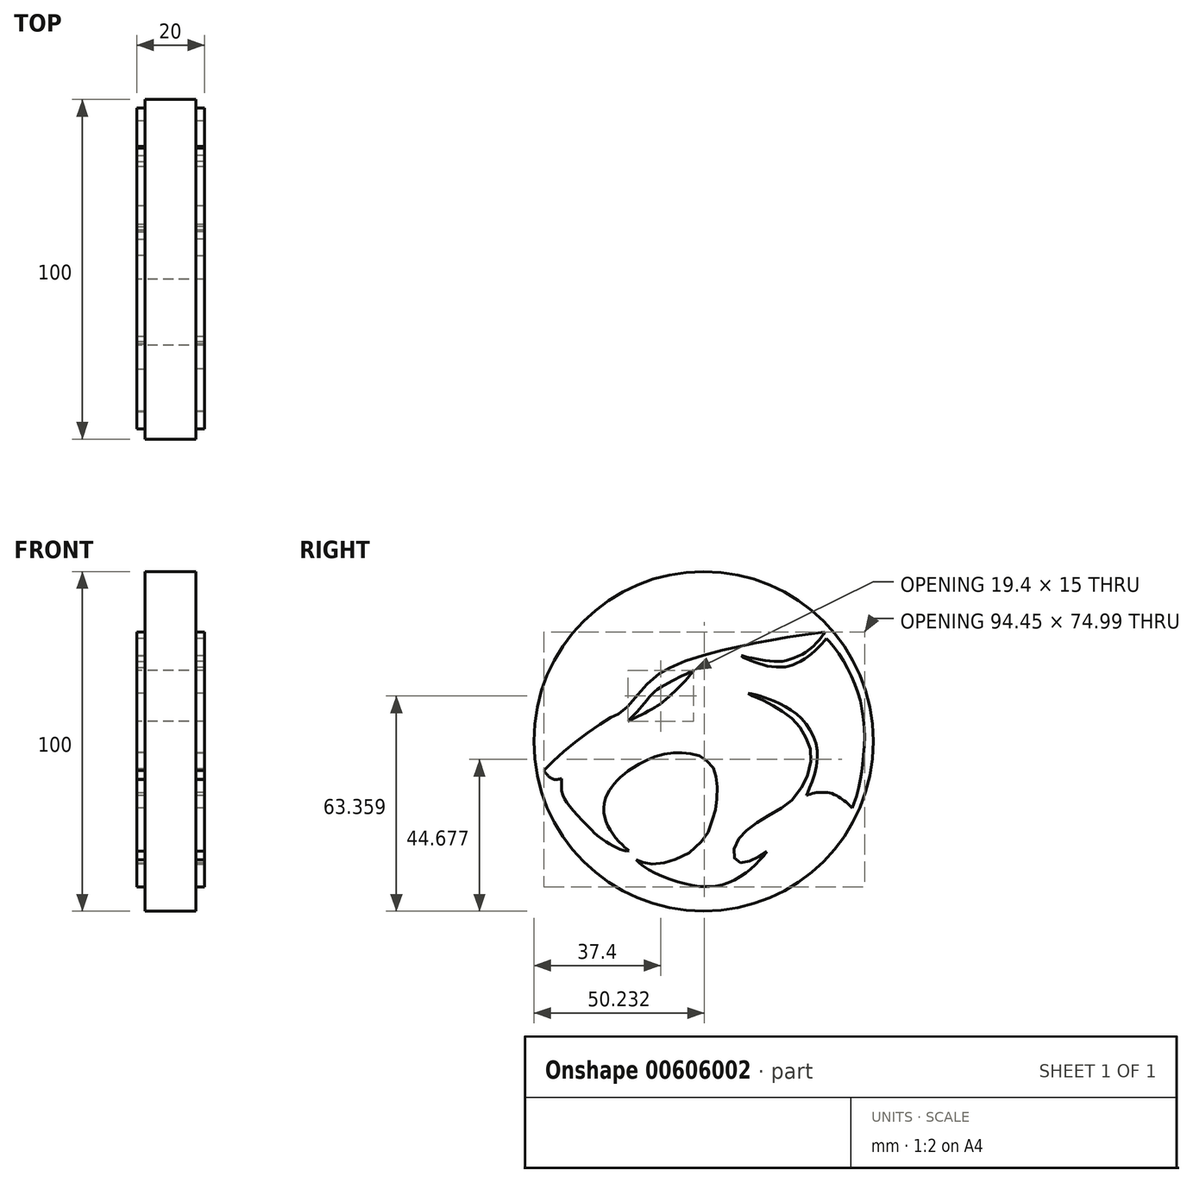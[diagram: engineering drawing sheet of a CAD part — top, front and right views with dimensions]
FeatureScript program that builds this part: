
annotation { "Feature Type Name" : "Feature", "Feature Type Description" : "" }
export const myFeature = defineFeature(function(context is Context, id is Id, definition is map)
    precondition{}
    {
        {
            var Q0;
            Q0=qCreatedBy(makeId("Right.planeOp"),FACE);
            var sketch = newSketch(context, id + "F0", { "sketchPlane" : qUnion([Q0])});
            skCircle(sketch, "E0", {"center": v(0, 0) * mm, "radius": 50 * mm});
            skFitSpline(sketch, "E1", {"points": [v(-47, -8.54) * mm, v(-41.27, -3.01) * mm, v(-33.53, 2.84) * mm, v(-26.97, 7.17) * mm, v(-24.14, 8.62) * mm, v(-17.89, 15.56) * mm, v(-14.85, 18.45) * mm, v(-13.16, 19.9) * mm, v(-4.4, 23.97) * mm, v(10.54, 27.95) * mm, v(20.91, 30.01) * mm, v(30.83, 31.56) * mm, v(35.72, 32.17) * mm], "startDerivative": vector(63.08, 64.93) * mm, "endDerivative": vector(65.23, 7.56) * mm});
            skFitSpline(sketch, "E2", {"points": [v(11.5, 25.21) * mm, v(13.68, 24.63) * mm, v(18.43, 23.8) * mm, v(22.9, 23.56) * mm, v(26.84, 24.6) * mm, v(31, 26.89) * mm, v(34.48, 30.36) * mm, v(35.72, 32.17) * mm], "startDerivative": vector(17.69, -5.27) * mm, "endDerivative": vector(9.54, 15.4) * mm});
            skFitSpline(sketch, "E3", {"points": [v(13.14, 14.17) * mm, v(14.47, 13.97) * mm, v(17.4, 13.1) * mm, v(20.48, 12) * mm, v(25.02, 9.67) * mm, v(29.51, 5.97) * mm, v(32.9, 0) * mm, v(33.22, -7.42) * mm, v(31.03, -14.2) * mm, v(30.28, -15.9) * mm], "startDerivative": vector(19.34, -1.93) * mm, "endDerivative": vector(-8.86, -19.07) * mm});
            skFitSpline(sketch, "E4", {"points": [v(-22.3, 5.86) * mm, v(-21.18, 7.13) * mm, v(-19.39, 8.93) * mm, v(-17.72, 10.93) * mm, v(-16.02, 13.02) * mm, v(-15.04, 14.03) * mm, v(-13.95, 15.09) * mm, v(-11.07, 16.79) * mm, v(-8.15, 18.4) * mm, v(-5.97, 19.46) * mm, v(-2.9, 20.86) * mm], "startDerivative": vector(12.35, 14.79) * mm, "endDerivative": vector(27.45, 12.44) * mm});
            skFitSpline(sketch, "E5", {"points": [v(-22.3, 5.86) * mm, v(-20.42, 6.83) * mm, v(-18.41, 7.74) * mm, v(-15.4, 9.41) * mm, v(-13.07, 10.75) * mm, v(-10.58, 12.84) * mm, v(-7.48, 15.7) * mm, v(-4.14, 19.34) * mm, v(-2.9, 20.86) * mm], "startDerivative": vector(18.07, 9.78) * mm, "endDerivative": vector(10.6, 13.27) * mm});
            skFitSpline(sketch, "E6", {"points": [v(18.64, -32.46) * mm, v(17.35, -33.2) * mm, v(16.28, -33.91) * mm, v(14.9, -34.66) * mm, v(13.55, -35.2) * mm, v(12.48, -35.57) * mm, v(11.07, -35.7) * mm, v(10.2, -35.55) * mm, v(9.43, -34.96) * mm, v(8.98, -34.07) * mm, v(8.84, -32.77) * mm, v(9.1, -31.39) * mm, v(9.66, -29.73) * mm, v(11.18, -27.66) * mm, v(12.32, -26.54) * mm, v(13.78, -25.3) * mm, v(15.96, -23.79) * mm, v(18.21, -22.4) * mm, v(20.99, -20.81) * mm, v(24.04, -19.04) * mm, v(25.8, -17.63) * mm, v(28, -14.8) * mm, v(29.63, -12.08) * mm, v(30.68, -9.85) * mm, v(31.54, -6.48) * mm, v(31.68, -3.98) * mm, v(31.38, -1.73) * mm, v(30.72, 0) * mm, v(29.68, 2.05) * mm, v(28.47, 4.07) * mm, v(27.15, 5.55) * mm, v(25.42, 7.23) * mm, v(23.8, 8.4) * mm, v(22.15, 9.49) * mm, v(20.94, 10.28) * mm, v(19, 11.3) * mm, v(17.3, 12.12) * mm, v(15.46, 12.94) * mm, v(13.94, 13.58) * mm, v(12.53, 14.01) * mm, v(13.14, 14.17) * mm], "startDerivative": vector(-61.1, -33.9) * mm, "endDerivative": vector(65.82, 9.84) * mm});
            skFitSpline(sketch, "E7", {"points": [v(-41.84, -10.98) * mm, v(-42.37, -11.12) * mm, v(-43.11, -11.2) * mm, v(-44.1, -11.17) * mm, v(-44.8, -10.9) * mm, v(-45.56, -10.4) * mm, v(-46.17, -9.75) * mm, v(-46.76, -8.97) * mm, v(-47, -8.54) * mm], "startDerivative": vector(-4.88, -1.53) * mm, "endDerivative": vector(-1.94, 4) * mm});
            skFitSpline(sketch, "E8", {"points": [v(-41.84, -10.98) * mm, v(-41.84, -12.08) * mm, v(-41.84, -14.06) * mm, v(-41.33, -16.15) * mm, v(-40.55, -17.67) * mm, v(-38.86, -19.79) * mm, v(-36.08, -22.97) * mm, v(-32.64, -26.4) * mm, v(-32.21, -26.92) * mm, v(-30, -28.62) * mm, v(-28.17, -29.85) * mm, v(-26.68, -30.76) * mm, v(-25.14, -31.5) * mm, v(-23.96, -32) * mm, v(-23.16, -32.23) * mm, v(-21.96, -32.28) * mm, v(-21.96, -32.25) * mm], "startDerivative": vector(0.4, -20.51) * mm, "endDerivative": vector(-1.88, 3.84) * mm});
            skFitSpline(sketch, "E9", {"points": [v(30.28, -15.9) * mm, v(31.64, -15.5) * mm, v(32.94, -15.1) * mm, v(34.3, -15.06) * mm, v(35.98, -15.01) * mm, v(37.38, -15.2) * mm, v(39.01, -15.9) * mm, v(40.46, -16.8) * mm, v(41.71, -17.7) * mm, v(43.01, -18.91) * mm, v(43.74, -19.69) * mm], "startDerivative": vector(14.08, 3.94) * mm, "endDerivative": vector(7.83, -8.61) * mm});
            skFitSpline(sketch, "E10", {"points": [v(43.74, -19.69) * mm, v(44.41, -17.9) * mm, v(45.71, -13.66) * mm, v(46.48, -9.47) * mm, v(46.92, -5.8) * mm, v(47.45, 0) * mm, v(47.3, 3.93) * mm, v(47.06, 6.27) * mm, v(46.58, 10) * mm, v(45.57, 14.17) * mm, v(43.74, 18.73) * mm, v(41.62, 22.97) * mm, v(39.01, 26.97) * mm, v(37, 29.47) * mm, v(36.22, 30.34) * mm], "startDerivative": vector(12.34, 31.34) * mm, "endDerivative": vector(-24.32, 23.64) * mm});
            skPoint(sketch, "E11.14.internal.orphan", {"position": v(0, -28.75) * mm});
            skFitSpline(sketch, "E12", {"points": [v(-19.85, -34.81) * mm, v(-19.42, -35.01) * mm, v(-18.54, -35.36) * mm, v(-17.77, -35.59) * mm, v(-16.77, -35.83) * mm, v(-15.49, -36.05) * mm, v(-13.17, -36.07) * mm, v(-11.35, -35.69) * mm, v(-9.64, -35.25) * mm, v(-7.52, -34.42) * mm, v(-4.55, -32.97) * mm, v(-1.22, -30.08) * mm, v(0, -28.75) * mm, v(1.13, -27.05) * mm, v(2.05, -24.76) * mm, v(2.84, -22.29) * mm, v(3.18, -21.15) * mm, v(3.55, -19.8) * mm, v(3.76, -18.3) * mm, v(4, -16.32) * mm, v(4.03, -14.35) * mm, v(4.03, -12.57) * mm, v(3.8, -10.88) * mm, v(3.5, -9.81) * mm, v(3.28, -8.7) * mm, v(2.74, -7.65) * mm, v(1.84, -6.56) * mm, v(0.8, -5.59) * mm, v(0, -4.94) * mm, v(-0.83, -4.5) * mm, v(-2.06, -3.98) * mm, v(-3.28, -3.67) * mm, v(-4.33, -3.5) * mm, v(-5.44, -3.33) * mm, v(-6.5, -3.3) * mm, v(-7.49, -3.3) * mm, v(-8.37, -3.33) * mm, v(-9.27, -3.33) * mm, v(-10.59, -3.54) * mm, v(-11.83, -3.79) * mm, v(-13.23, -4.07) * mm, v(-14.57, -4.53) * mm, v(-15.35, -4.92) * mm, v(-16.2, -5.32) * mm, v(-17.36, -5.85) * mm, v(-18.31, -6.31) * mm, v(-19.33, -6.89) * mm, v(-20.26, -7.48) * mm, v(-21.28, -8.1) * mm], "startDerivative": vector(31.55, -15.53) * mm, "endDerivative": vector(-54.06, -32.07) * mm});
            skFitSpline(sketch, "E13", {"points": [v(-21.96, -32.25) * mm, v(-22.15, -32.04) * mm, v(-22.58, -31.69) * mm, v(-23.05, -31.3) * mm, v(-23.35, -31.1) * mm, v(-23.82, -30.58) * mm, v(-24.6, -29.82) * mm, v(-25.66, -28.75) * mm, v(-26.48, -27.56) * mm, v(-27.02, -26.78) * mm, v(-27.69, -25.78) * mm, v(-28.36, -24.42) * mm, v(-28.76, -23.33) * mm, v(-29.1, -22.07) * mm, v(-29.33, -21.17) * mm, v(-29.37, -19.83) * mm, v(-29.33, -18.67) * mm, v(-28.99, -17.2) * mm, v(-28.5, -16.05) * mm, v(-28.13, -15.19) * mm, v(-27.55, -14.23) * mm, v(-27.04, -13.48) * mm, v(-26.48, -12.72) * mm, v(-25.75, -11.82) * mm, v(-24.8, -10.86) * mm, v(-23.82, -9.97) * mm, v(-22.85, -9.22) * mm, v(-21.96, -8.57) * mm, v(-21.28, -8.1) * mm], "startDerivative": vector(-9.04, 10.86) * mm, "endDerivative": vector(20.53, 14.33) * mm});
            skFitSpline(sketch, "E14", {"points": [v(-19.85, -34.81) * mm, v(-19.42, -35.42) * mm, v(-18.37, -36.25) * mm, v(-17.87, -36.7) * mm, v(-16.93, -37.33) * mm, v(-15.27, -38.32) * mm, v(-13.57, -39.13) * mm, v(-11.46, -39.98) * mm, v(-9.11, -40.9) * mm, v(-7.02, -41.52) * mm, v(-5.14, -42.03) * mm, v(-3.05, -42.37) * mm, v(-1.05, -42.72) * mm, v(-0.26, -42.78) * mm, v(0.57, -42.82) * mm, v(1.73, -42.8) * mm, v(3.35, -42.72) * mm, v(5.07, -42.33) * mm, v(6.37, -41.93) * mm, v(7.93, -41.34) * mm, v(9.17, -40.75) * mm, v(10.6, -39.92) * mm, v(12.2, -38.95) * mm, v(13.06, -38.24) * mm, v(14.3, -37.25) * mm, v(15.45, -36.11) * mm, v(16.32, -35.24) * mm, v(17.3, -34.17) * mm, v(18.02, -33.3) * mm, v(18.64, -32.46) * mm], "startDerivative": vector(13.2, -24.31) * mm, "endDerivative": vector(21.16, 29.2) * mm});
            skFitSpline(sketch, "E15", {"points": [v(36.22, 30.34) * mm, v(35.8, 29.8) * mm, v(35, 28.87) * mm, v(34.08, 27.86) * mm, v(32.78, 26.68) * mm, v(31.49, 25.57) * mm, v(30.45, 24.8) * mm, v(29.45, 24.1) * mm, v(28.01, 23.3) * mm, v(27, 22.79) * mm, v(25.9, 22.34) * mm, v(24.46, 21.97) * mm, v(23.68, 21.9) * mm, v(22.06, 21.83) * mm, v(20.59, 21.93) * mm, v(19.11, 22.1) * mm, v(17.9, 22.42) * mm, v(16.42, 22.88) * mm, v(15.23, 23.3) * mm, v(13.79, 23.8) * mm, v(12.5, 24.3) * mm, v(11.5, 24.72) * mm, v(11.07, 25.21) * mm, v(11.1, 25.21) * mm], "startDerivative": vector(-11.39, -15.25) * mm, "endDerivative": vector(6.44, -1.74) * mm});
            skFitSpline(sketch, "E16", {"points": [v(11.5, 25.21) * mm, v(11.1, 25.21) * mm], "startDerivative": vector(-0.4, 0) * mm, "endDerivative": vector(-0.4, 0) * mm});
            skSolve(sketch);
        }
        {
            var Q0;
            Q0=makeQuery(id+"F0.imprint","IMPRINT",FACE,{"disambiguationData":[TD([[makeQuery(id+"F0.imprint","IMPRINT",EDGE,{"derivedFrom":sQuery(id+"F0.wireOp",EDGE,"E1")}),-1.0]])]});
            extrude(context, id + "F1", {"entities" : qUnion([Q0]), "endBound" : BoundingType.SYMMETRIC, "depth" : 20 * mm, "offsetDistance" : 25 * mm});
        }
        {
            var Q0;
            Q0=makeQuery(id+"F0.imprint","IMPRINT",FACE,{"disambiguationData":[TD([[makeQuery(id+"F0.imprint","IMPRINT",EDGE,{"derivedFrom":sQuery(id+"F0.wireOp",EDGE,"E0")}),1.0]])]});
            extrude(context, id + "F2", {"entities" : qUnion([Q0]), "operationType" : NewBodyOperationType.ADD, "endBound" : BoundingType.SYMMETRIC, "depth" : 15 * mm, "offsetDistance" : 25 * mm});
        }
    });
